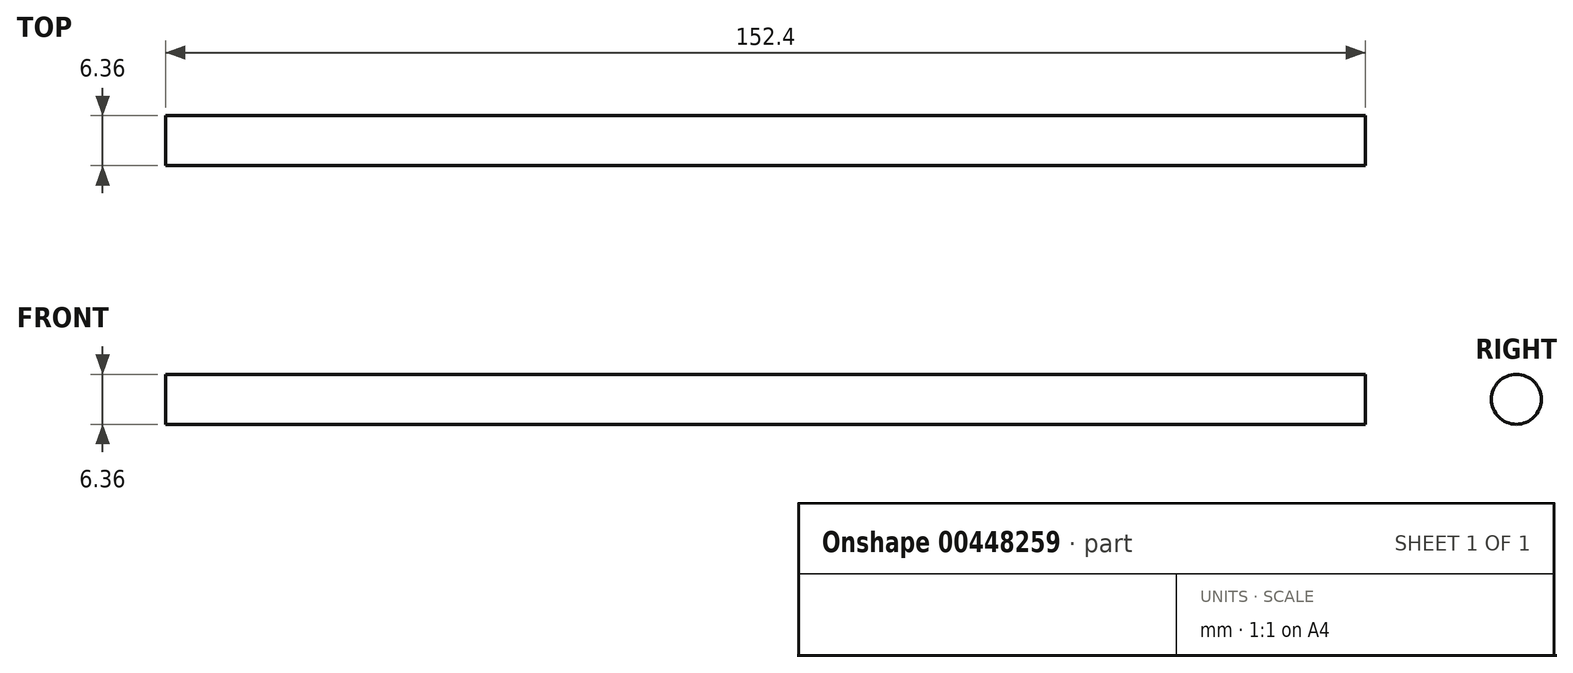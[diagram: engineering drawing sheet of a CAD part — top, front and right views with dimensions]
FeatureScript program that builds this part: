
annotation { "Feature Type Name" : "Feature", "Feature Type Description" : "" }
export const myFeature = defineFeature(function(context is Context, id is Id, definition is map)
    precondition{}
    {
        {
            var Q0;
            Q0=qCreatedBy(makeId("Right.planeOp"),FACE);
            var sketch = newSketch(context, id + "F0", { "sketchPlane" : qUnion([Q0])});
            skCircle(sketch, "E0", {"center": v(0, 0) * mm, "radius": 3.18 * mm});
            skSolve(sketch);
        }
        {
            var Q0;
            Q0=makeQuery(id+"F0.imprint","IMPRINT",FACE,{"disambiguationData":[TD([[makeQuery(id+"F0.imprint","IMPRINT",EDGE,{"derivedFrom":sQuery(id+"F0.wireOp",EDGE,"E0")}),1.0]])]});
            extrude(context, id + "F1", {"entities" : qUnion([Q0]), "depth" : 152.4 * mm});
        }
    });
